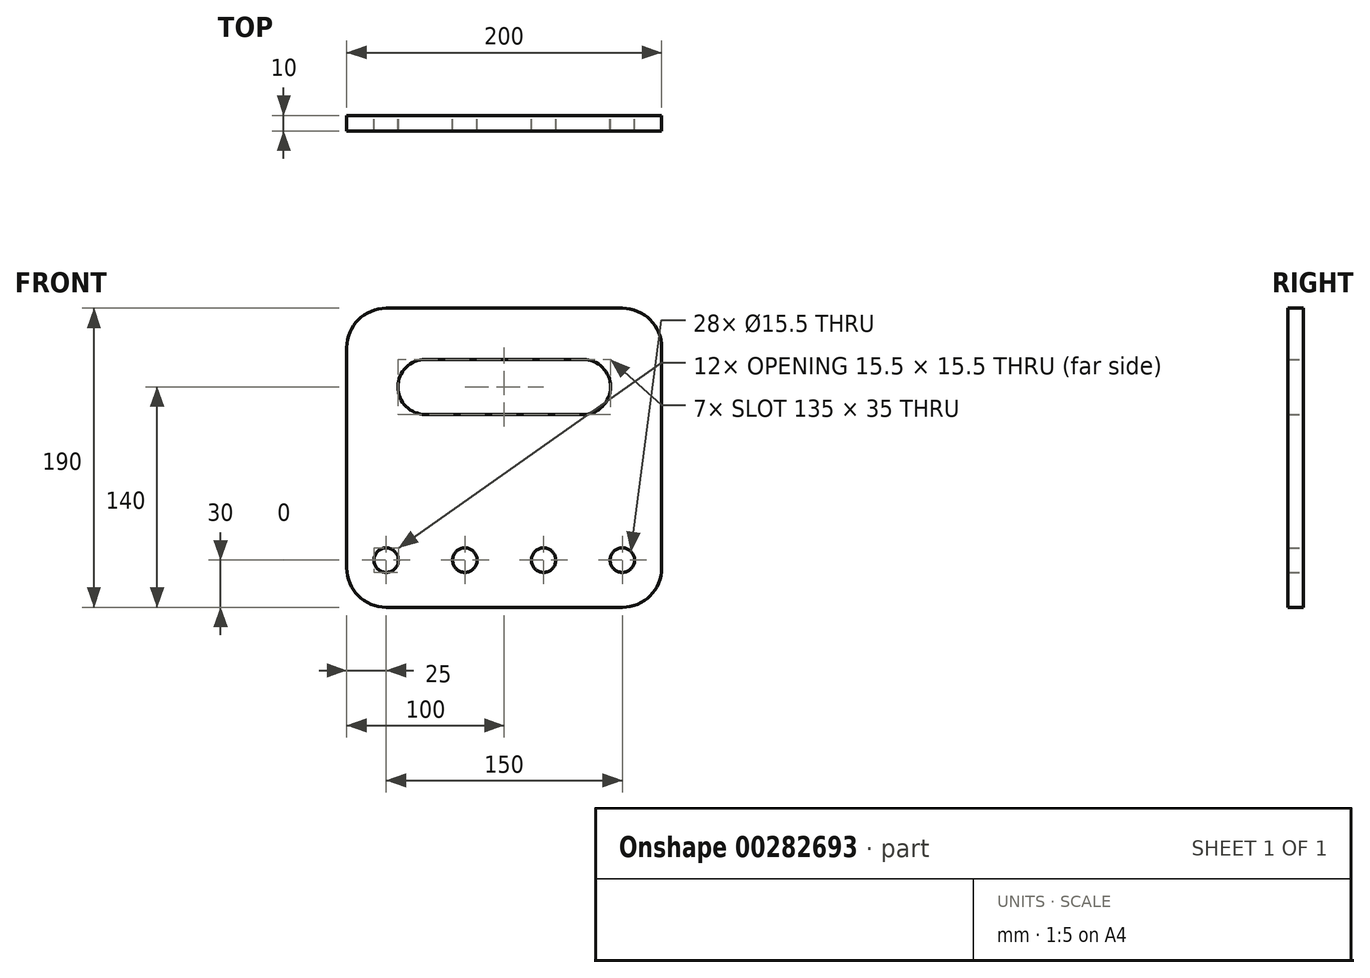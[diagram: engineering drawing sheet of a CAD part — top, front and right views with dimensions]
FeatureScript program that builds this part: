
annotation { "Feature Type Name" : "Feature", "Feature Type Description" : "" }
export const myFeature = defineFeature(function(context is Context, id is Id, definition is map)
    precondition{}
    {
        {
            var Q0;
            Q0=qCreatedBy(makeId("Front.planeOp"),FACE);
            var sketch = newSketch(context, id + "F0", { "sketchPlane" : qUnion([Q0])});
            skLineSegment(sketch, "E0.bottom", {"start": v(-100, 95) * mm, "end": v(100, 95) * mm});
            skLineSegment(sketch, "E0.top", {"start": v(-100, -95) * mm, "end": v(100, -95) * mm});
            skLineSegment(sketch, "E0.left", {"start": v(-100, 95) * mm, "end": v(-100, -95) * mm});
            skLineSegment(sketch, "E0.right", {"start": v(100, 95) * mm, "end": v(100, -95) * mm});
            skPoint(sketch, "E0.middle", {"position": v(0, 0) * mm});
            skLineSegment(sketch, "E1", {"start": v(-113.43, 45) * mm, "end": v(119.98, 45) * mm, "construction": true});
            skArc(sketch, "E2", {"start": v(-50, 62.5) * mm, "mid": v(-67.5, 45) * mm, "end": v(-50, 27.5) * mm});
            skArc(sketch, "E3", {"start": v(50, 27.5) * mm, "mid": v(67.5, 45) * mm, "end": v(50, 62.5) * mm});
            skLineSegment(sketch, "E4", {"start": v(-50, 27.5) * mm, "end": v(50, 27.5) * mm});
            skLineSegment(sketch, "E5.trimOffspring", {"start": v(-50, 62.5) * mm, "end": v(50, 62.5) * mm});
            skSolve(sketch);
        }
        {
            var Q0;
            Q0=makeQuery(id+"F0.imprint","IMPRINT",FACE,{"disambiguationData":[TD([[makeQuery(id+"F0.imprint","IMPRINT",EDGE,{"derivedFrom":sQuery(id+"F0.wireOp",EDGE,"E0.bottom")}),-1.0]])]});
            extrude(context, id + "F1", {"entities" : qUnion([Q0]), "depth" : 10 * mm});
        }
        {
            var Q0;
            Q0=makeQuery(id+"F1.opExtrude","CAP_FACE",FACE,{"disambiguationData":[OSD([sQuery(id+"F0.wireOp",EDGE,"E0.bottom"),sQuery(id+"F0.wireOp",EDGE,"E0.top"),sQuery(id+"F0.wireOp",EDGE,"E0.left"),sQuery(id+"F0.wireOp",EDGE,"E0.right"),sQuery(id+"F0.wireOp",EDGE,"E2"),sQuery(id+"F0.wireOp",EDGE,"E3"),sQuery(id+"F0.wireOp",EDGE,"E4"),sQuery(id+"F0.wireOp",EDGE,"E5.trimOffspring")])],"isStart":false});
            var sketch = newSketch(context, id + "F2", { "sketchPlane" : qUnion([Q0])});
            skPoint(sketch, "E6", {"position": v(75, -65) * mm});
            skPoint(sketch, "E7", {"position": v(25, -65) * mm});
            skPoint(sketch, "E8", {"position": v(-25, -65) * mm});
            skPoint(sketch, "E9", {"position": v(-75, -65) * mm});
            skSolve(sketch);
        }
        {
            var Q0;
            Q0=sQuery(id+"F2.wireOp",VERTEX,"E9");
            var Q1;
            Q1=sQuery(id+"F2.wireOp",VERTEX,"E8");
            var Q2;
            Q2=sQuery(id+"F2.wireOp",VERTEX,"E7");
            var Q3;
            Q3=sQuery(id+"F2.wireOp",VERTEX,"E6");
            var Q4;
            Q4=makeQuery(id+"F1.opExtrude","SWEPT_BODY",BODY,{"disambiguationData":[OSD([sQuery(id+"F0.wireOp",EDGE,"E0.bottom"),sQuery(id+"F0.wireOp",EDGE,"E0.top"),sQuery(id+"F0.wireOp",EDGE,"E0.left"),sQuery(id+"F0.wireOp",EDGE,"E0.right"),sQuery(id+"F0.wireOp",EDGE,"E2"),sQuery(id+"F0.wireOp",EDGE,"E3"),sQuery(id+"F0.wireOp",EDGE,"E4"),sQuery(id+"F0.wireOp",EDGE,"E5.trimOffspring")])]});
            hole(context, id + "F3", {"style" : HoleStyle.SIMPLE, "endStyle" : HoleEndStyle.THROUGH, "holeDiameter" : 15.5 * mm, "tappedDepth" : 12 * mm, "tapClearance" : 3, "locations" : qUnion([Q0, Q1, Q2, Q3]), "scope" : qUnion([Q4]), "startStyle" : HoleStartStyle.PART});
        }
        {
            var Q0;
            Q0=makeQuery(id+"F1.opExtrude","SWEPT_EDGE",EDGE,{"disambiguationData":[OSD([sQuery(id+"F0.wireOp",EDGE,"E0.bottom"),sQuery(id+"F0.wireOp",EDGE,"E0.right")])]});
            var Q1;
            Q1=makeQuery(id+"F1.opExtrude","SWEPT_EDGE",EDGE,{"disambiguationData":[OSD([sQuery(id+"F0.wireOp",EDGE,"E0.bottom"),sQuery(id+"F0.wireOp",EDGE,"E0.left")])]});
            var Q2;
            Q2=makeQuery(id+"F1.opExtrude","SWEPT_EDGE",EDGE,{"disambiguationData":[OSD([sQuery(id+"F0.wireOp",EDGE,"E0.top"),sQuery(id+"F0.wireOp",EDGE,"E0.right")])]});
            var Q3;
            Q3=makeQuery(id+"F1.opExtrude","SWEPT_EDGE",EDGE,{"disambiguationData":[OSD([sQuery(id+"F0.wireOp",EDGE,"E0.top"),sQuery(id+"F0.wireOp",EDGE,"E0.left")])]});
            fillet(context, id + "F4", {"entities" : qUnion([Q0, Q1, Q2, Q3]), "radius" : 25 * mm, "tangentPropagation" : true, "allowEdgeOverflow" : false});
        }
    });
